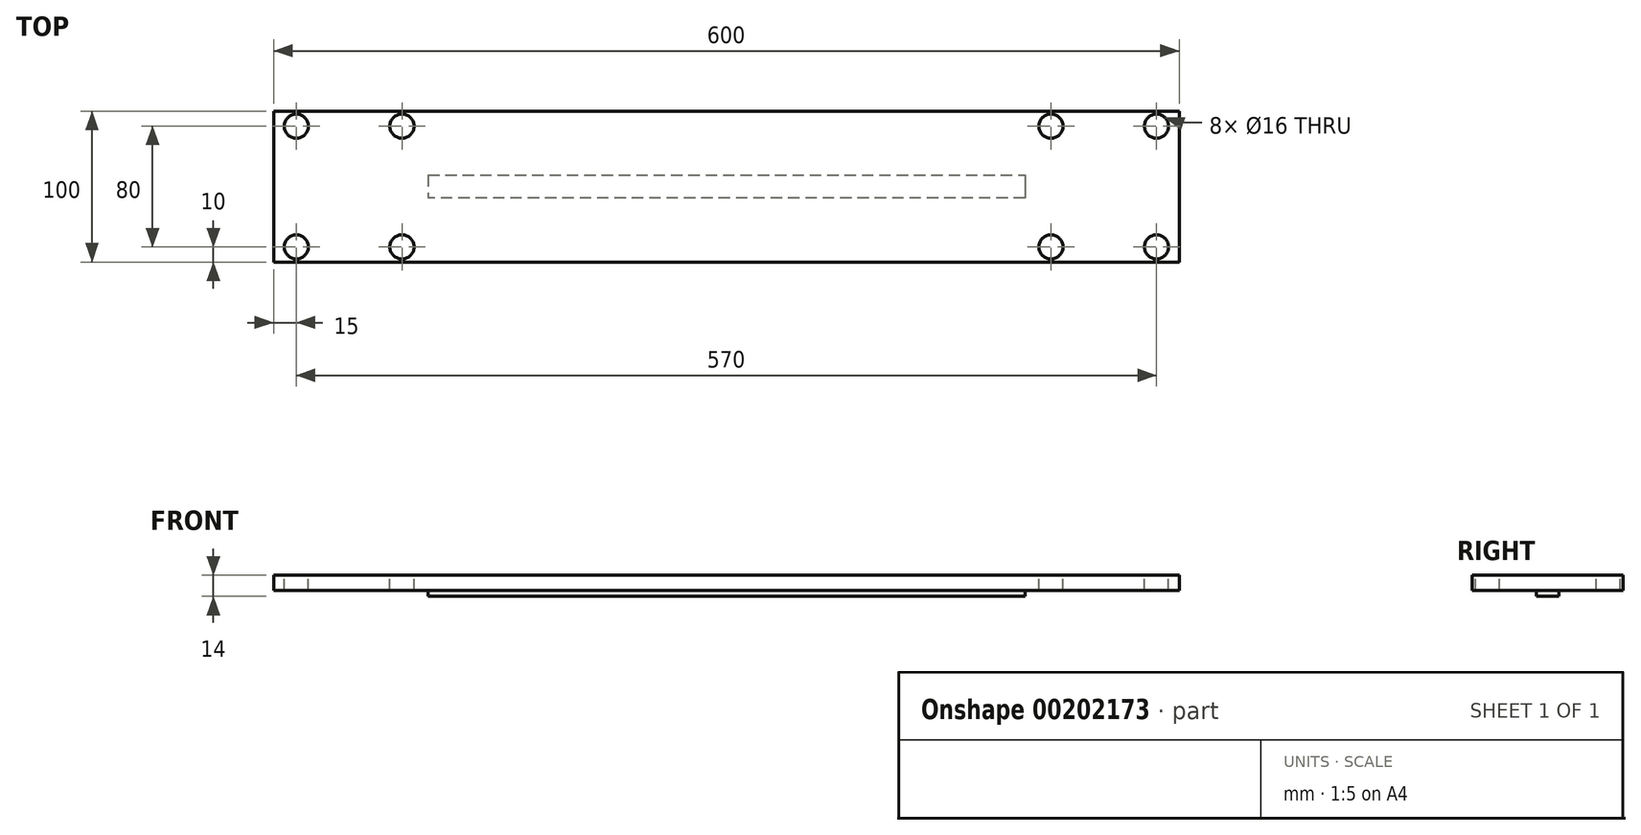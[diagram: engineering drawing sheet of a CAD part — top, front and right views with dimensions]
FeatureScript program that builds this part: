
annotation { "Feature Type Name" : "Feature", "Feature Type Description" : "" }
export const myFeature = defineFeature(function(context is Context, id is Id, definition is map)
    precondition{}
    {
        {
            var Q0;
            Q0=qCreatedBy(makeId("Front.planeOp"),FACE);
            var sketch = newSketch(context, id + "F0", { "sketchPlane" : qUnion([Q0])});
            skLineSegment(sketch, "E0", {"start": v(0, 0) * mm, "end": v(600, 0) * mm});
            skLineSegment(sketch, "E1", {"start": v(600, 0) * mm, "end": v(600, -10) * mm});
            skLineSegment(sketch, "E2", {"start": v(600, -10) * mm, "end": v(530, -10) * mm});
            skLineSegment(sketch, "E3", {"start": v(0, -10) * mm, "end": v(0, 0) * mm});
            skLineSegment(sketch, "E4", {"start": v(0, -10) * mm, "end": v(70, -10) * mm, "construction": true});
            skLineSegment(sketch, "E5", {"start": v(600, -10) * mm, "end": v(530, -10) * mm, "construction": true});
            skLineSegment(sketch, "E6.trimOffspring", {"start": v(70, -10) * mm, "end": v(0, -10) * mm});
            skLineSegment(sketch, "E7", {"start": v(70, -10) * mm, "end": v(530, -10) * mm});
            skSolve(sketch);
        }
        {
            var Q0;
            Q0=qSketchRegion(id+"F0",true);
            extrude(context, id + "F1", {"entities" : qUnion([Q0]), "depth" : 100 * mm});
        }
        {
            var Q0;
            Q0=makeQuery(id+"F1.opExtrude","SWEPT_FACE",FACE,{"disambiguationData":[OSD([sQuery(id+"F0.wireOp",EDGE,"E0")])]});
            var sketch = newSketch(context, id + "F2", { "sketchPlane" : qUnion([Q0])});
            skLineSegment(sketch, "E8", {"start": v(0, -50) * mm, "end": v(100, -50) * mm, "construction": true});
            skLineSegment(sketch, "E9.bottom", {"start": v(85, -90) * mm, "end": v(15, -90) * mm});
            skLineSegment(sketch, "E9.top", {"start": v(85, -10) * mm, "end": v(15, -10) * mm});
            skLineSegment(sketch, "E9.left", {"start": v(85, -90) * mm, "end": v(85, -10) * mm});
            skLineSegment(sketch, "E9.right", {"start": v(15, -90) * mm, "end": v(15, -10) * mm});
            skPoint(sketch, "E9.middle", {"position": v(50, -50) * mm});
            skLineSegment(sketch, "E10", {"start": v(600, -50) * mm, "end": v(500, -50) * mm, "construction": true});
            skLineSegment(sketch, "E11.bottom", {"start": v(585, -90) * mm, "end": v(515, -90) * mm});
            skLineSegment(sketch, "E11.top", {"start": v(585, -10) * mm, "end": v(515, -10) * mm});
            skLineSegment(sketch, "E11.left", {"start": v(585, -90) * mm, "end": v(585, -10) * mm});
            skLineSegment(sketch, "E11.right", {"start": v(515, -90) * mm, "end": v(515, -10) * mm});
            skPoint(sketch, "E11.middle", {"position": v(550, -50) * mm});
            skSolve(sketch);
        }
        {
            var Q0;
            Q0=sQuery(id+"F2.wireOp",VERTEX,"E9.top.end");
            var Q1;
            Q1=sQuery(id+"F2.wireOp",VERTEX,"E9.bottom.end");
            var Q2;
            Q2=sQuery(id+"F2.wireOp",VERTEX,"E9.top.start");
            var Q3;
            Q3=sQuery(id+"F2.wireOp",VERTEX,"E9.left.start");
            var Q4;
            Q4=sQuery(id+"F2.wireOp",VERTEX,"E11.top.end");
            var Q5;
            Q5=sQuery(id+"F2.wireOp",VERTEX,"E11.right.start");
            var Q6;
            Q6=sQuery(id+"F2.wireOp",VERTEX,"E11.left.start");
            var Q7;
            Q7=sQuery(id+"F2.wireOp",VERTEX,"E11.left.end");
            var Q8;
            Q8=makeQuery(id+"F1.opExtrude","SWEPT_BODY",BODY,{"disambiguationData":[OSD([sQuery(id+"F0.wireOp",EDGE,"E0"),sQuery(id+"F0.wireOp",EDGE,"E1"),sQuery(id+"F0.wireOp",EDGE,"E2"),sQuery(id+"F0.wireOp",EDGE,"E3"),sQuery(id+"F0.wireOp",EDGE,"7ojeD2Lx-nS1t-1hTE-gq8g-C9srDyLe6pUy"),sQuery(id+"F0.wireOp",EDGE,"rq3Mynzp-fh6F-mfEs-RFJS-R7UwMkgZCplj"),sQuery(id+"F0.wireOp",EDGE,"qSBE7008-Ep3j-znpi-jIoY-ObV4W3xdA1eV"),sQuery(id+"F0.wireOp",EDGE,"E6.trimOffspring")])]});
            hole(context, id + "F3", {"style" : HoleStyle.SIMPLE, "endStyle" : HoleEndStyle.THROUGH, "holeDiameter" : 16 * mm, "locations" : qUnion([Q0, Q1, Q2, Q3, Q4, Q5, Q6, Q7]), "scope" : qUnion([Q8]), "isTappedThrough" : true});
        }
        {
            var Q0;
            Q0=makeQuery(id+"F1.opExtrude","SWEPT_FACE",FACE,{"disambiguationData":[OSD([sQuery(id+"F0.wireOp",EDGE,"E2"),sQuery(id+"F0.wireOp",EDGE,"E6.trimOffspring"),sQuery(id+"F0.wireOp",EDGE,"E7")])]});
            var sketch = newSketch(context, id + "F4", { "sketchPlane" : qUnion([Q0])});
            skLineSegment(sketch, "E12", {"start": v(0, 50) * mm, "end": v(600, 50) * mm, "construction": true});
            skLineSegment(sketch, "E13", {"start": v(93, 90.34) * mm, "end": v(102.3, 90.34) * mm, "construction": true});
            skLineSegment(sketch, "E14", {"start": v(102.3, 90.34) * mm, "end": v(102.3, 50) * mm, "construction": true});
            skLineSegment(sketch, "E15", {"start": v(507, 89.78) * mm, "end": v(497.7, 89.75) * mm, "construction": true});
            skLineSegment(sketch, "E16", {"start": v(497.7, 89.75) * mm, "end": v(497.85, 50) * mm, "construction": true});
            skLineSegment(sketch, "E17", {"start": v(102.3, 50) * mm, "end": v(102.3, 57.5) * mm});
            skLineSegment(sketch, "E18", {"start": v(102.3, 50) * mm, "end": v(102.3, 42.5) * mm});
            skLineSegment(sketch, "E19", {"start": v(102.3, 42.5) * mm, "end": v(497.85, 42.5) * mm});
            skLineSegment(sketch, "E20", {"start": v(497.85, 42.5) * mm, "end": v(497.85, 50) * mm});
            skLineSegment(sketch, "E21", {"start": v(497.85, 50) * mm, "end": v(497.83, 57.5) * mm});
            skLineSegment(sketch, "E22", {"start": v(497.83, 57.5) * mm, "end": v(102.3, 57.5) * mm});
            skSolve(sketch);
        }
        {
            var Q0;
            Q0=qSketchRegion(id+"F4",true);
            extrude(context, id + "F5", {"entities" : qUnion([Q0]), "operationType" : NewBodyOperationType.ADD, "depth" : 4 * mm});
        }
    });
